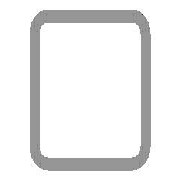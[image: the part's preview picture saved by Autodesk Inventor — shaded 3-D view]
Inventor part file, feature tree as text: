
AUTODESK INVENTOR PART (.ipt)
format: ipt  version: 2025 (Build 290162010, 162A)  size: 133,632 bytes
history: native  units: mm (DEFAULTED — no unit token found)
features: other x4, sketch x1, plane x1
ambient origin geometry x8: Origin, YZ Plane, XZ Plane, XY Plane, X Axis, Y Axis, Z Axis, Center Point
bodies: Solid1 (feature_tree), Body (feature_tree)
feature tree (6):
  parser-record x1  (decoder bookkeeping rows leaked as tree rows — omitted from the tree; the rows remain in map.json)
  other  "Driven Length"
  other  "Start Plane"
  other  "End Plane"
  sketch  "Sketch3"  dims[d3=898.0mm d4=0.0mm d7=4.0mm d9=40.0mm d11=40.0mm d12=2.0mm d13=-0.0mm d14=898.0mm d15=20.0mm d16=20.0mm d17=90.0deg d18=898.0mm]
  plane  "Work Plane3"
